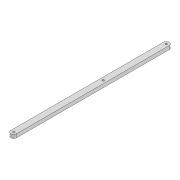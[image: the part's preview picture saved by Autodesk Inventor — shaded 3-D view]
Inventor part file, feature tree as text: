
AUTODESK INVENTOR PART (.ipt)
format: ipt  version: 2022 (Build 260153000, 153)  size: 90,112 bytes
history: native  units: mm
features: extrude x1, sketch x1
ambient origin geometry x8: Origin, YZ Plane, XZ Plane, XY Plane, X Axis, Y Axis, Z Axis, Center Point
bodies: Solid1 (feature_tree)
feature tree (2):
  extrude  "Extrusion1"  Depth=6.0mm
  sketch  "Sketch1"  dims[d0=3.3mm d1=3.3mm d2=10.0mm d3=261.6mm d4=3.3mm d5=153.559mm d6=6.0mm d7=0.0mm]
